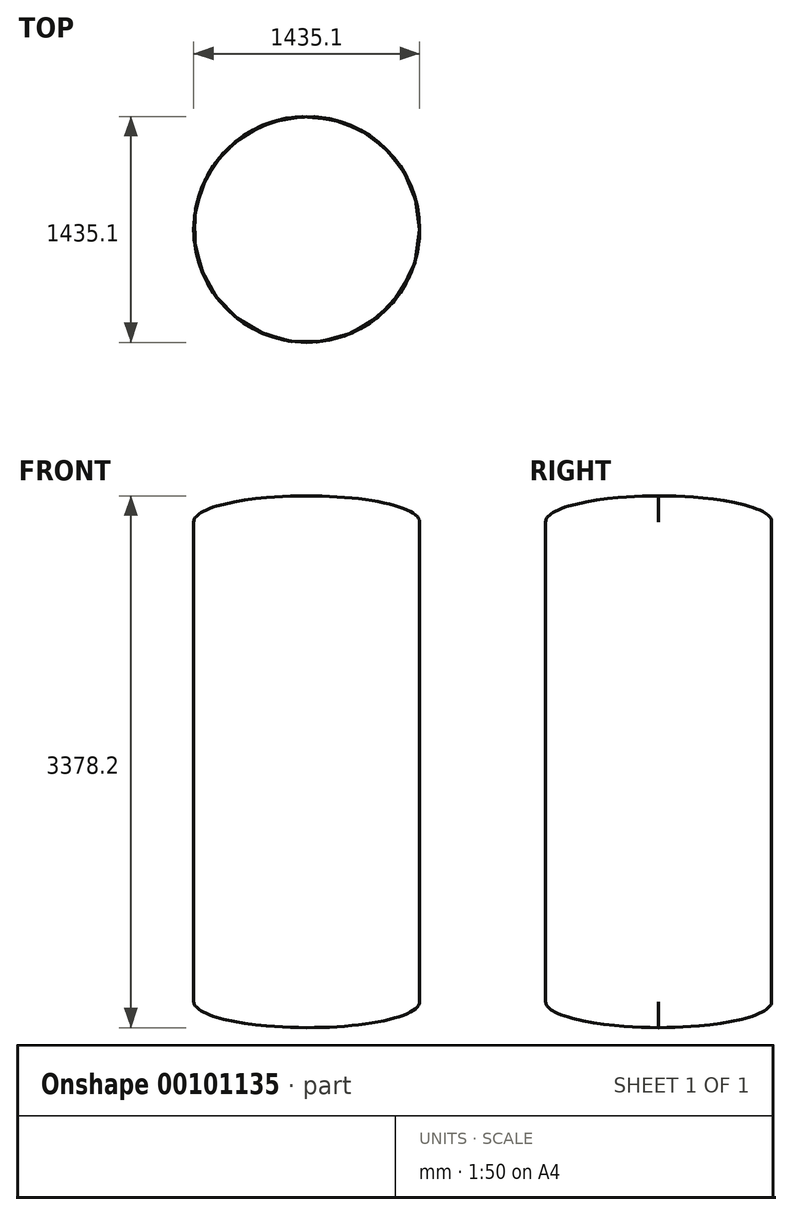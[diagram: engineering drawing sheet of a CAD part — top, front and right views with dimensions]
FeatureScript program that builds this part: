
annotation { "Feature Type Name" : "Feature", "Feature Type Description" : "" }
export const myFeature = defineFeature(function(context is Context, id is Id, definition is map)
    precondition{}
    {
        {
            var Q0;
            Q0=qCreatedBy(makeId("Front.planeOp"),FACE);
            var sketch = newSketch(context, id + "F0", { "sketchPlane" : qUnion([Q0])});
            skLineSegment(sketch, "E0", {"start": v(0, 2260.6) * mm, "end": v(0, -2260.6) * mm, "construction": true});
            skLineSegment(sketch, "E1", {"start": v(0, 0) * mm, "end": v(717.55, 0) * mm, "construction": true});
            skLineSegment(sketch, "E2", {"start": v(717.55, 1524) * mm, "end": v(717.55, -1524) * mm});
            skLineSegment(sketch, "E3", {"start": v(717.55, 1524) * mm, "end": v(0, 1524) * mm, "construction": true});
            skLineSegment(sketch, "E4", {"start": v(717.55, -1524) * mm, "end": v(0, -1524) * mm, "construction": true});
            skEllipticalArc(sketch, "E5", {});
            skEllipticalArc(sketch, "E6", {});
            const initialGuessF0  = {"E5": [0, 1.524, 1, 0, 0.71755, 0.1651, 0, 1.5707963267948966], "E6": [0, -1.524, 1, 0, 0.71755, 0.1651, 4.71238898038469, 0]};
            skSetInitialGuess(sketch, initialGuessF0);
            skSolve(sketch);
        }
        {
            var Q0;
            Q0=sQuery(id+"F0.wireOp",EDGE,"E5");
            var Q1;
            Q1=sQuery(id+"F0.wireOp",EDGE,"E2");
            var Q2;
            Q2=sQuery(id+"F0.wireOp",EDGE,"E6");
            var Q3;
            Q3=sQuery(id+"F0.wireOp",EDGE,"E0");
            revolve(context, id + "F1", {"bodyType" : ToolBodyType.SURFACE, "surfaceEntities" : qUnion([Q0, Q1, Q2]), "axis" : qUnion([Q3]), "revolveType" : RevolveType.FULL});
        }
    });
